# Revit family: Plumbing_Valves_TOTO-USA-Inc_EcoPowerR-Thermostatic-Mixing-Valve-for
name_source: partatom
category: Plumbing Fixtures
revit_build: Autodesk Revit 2015 (Build: 20140606_1530(x64)
units: mm (PartAtom-declared; Revit-internal decimal feet)

## types (1)
- TLT20
    Ambient Temp. = 32 - 104°F (0 - 40°C)
    Description = ASSE approved wax type Thermostatic Mixing Valve specially designed for TOTO 0.35 GPM EcoPower Faucets
    Humidity = Max. 90% RH
    Manufacturer = TOTO
    Material Plastic = Plastic - TOTO - White
    Material Steel = Metal - TOTO - Stainless Steel
    Model = TLT20
    Outlet Temp. = 100±4°F (38±2°C)
    Recommended Temp.Range = Hot Supply: 120 - 180°F (49 -82°C), Cold supply 39 - 80°F (4 - 27°C)
    URL = www.totousa.com
    Warranty = Three Year Limited
    Water Supply Connection = 0' - 0 1/2"
    Water Supply Pressure(Max) = 80.00 psi
    Water Supply Pressure(Min) = 15.00 psi

## geometry (parser evidence)
native form markers: Sweep x3
no freeform markers — native parametric forms only
